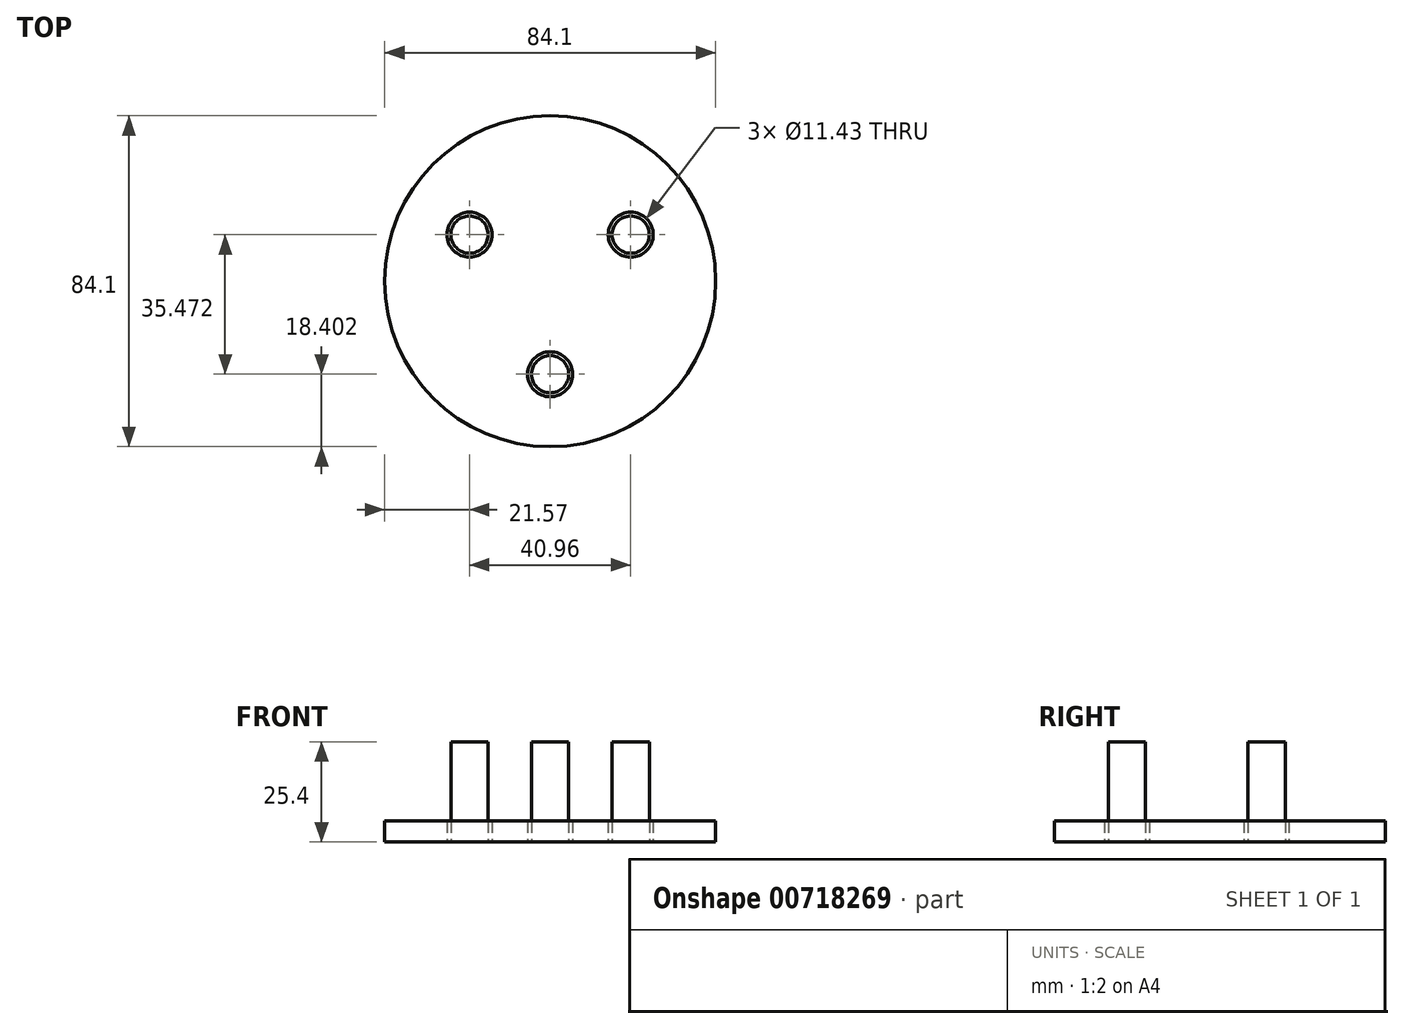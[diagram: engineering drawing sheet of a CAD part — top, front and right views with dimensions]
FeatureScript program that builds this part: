
annotation { "Feature Type Name" : "Feature", "Feature Type Description" : "" }
export const myFeature = defineFeature(function(context is Context, id is Id, definition is map)
    precondition{}
    {
        {
            var Q0;
            Q0=qCreatedBy(makeId("Top.planeOp"),FACE);
            var sketch = newSketch(context, id + "F0", { "sketchPlane" : qUnion([Q0])});
            skCircle(sketch, "E0", {"center": v(0, 0) * mm, "radius": 42.05 * mm});
            skSolve(sketch);
        }
        {
            var Q0;
            Q0=makeQuery(id+"F0.imprint","IMPRINT",FACE,{"disambiguationData":[TD([[makeQuery(id+"F0.imprint","IMPRINT",EDGE,{"derivedFrom":sQuery(id+"F0.wireOp",EDGE,"E0")}),1.0]])]});
            extrude(context, id + "F1", {"entities" : qUnion([Q0]), "depth" : 5.33 * mm, "offsetDistance" : 25.4 * mm});
        }
        {
            var Q0;
            Q0=qCreatedBy(makeId("Top.planeOp"),FACE);
            var sketch = newSketch(context, id + "F2", { "sketchPlane" : qUnion([Q0])});
            skCircle(sketch, "E1", {"center": v(-20.48, 11.82) * mm, "radius": 4.72 * mm});
            skCircle(sketch, "E2.cCircle", {"center": v(0, 0) * mm, "radius": 11.82 * mm, "construction": true});
            skLineSegment(sketch, "E2.0", {"start": v(-20.48, 11.82) * mm, "end": v(20.48, 11.82) * mm, "construction": true});
            skLineSegment(sketch, "E2.1", {"start": v(20.48, 11.82) * mm, "end": v(0, -23.65) * mm, "construction": true});
            skLineSegment(sketch, "E2.2", {"start": v(0, -23.65) * mm, "end": v(-20.48, 11.82) * mm, "construction": true});
            skPoint(sketch, "E2.0.midPoint", {"position": v(0, 11.82) * mm});
            skCircle(sketch, "E3", {"center": v(20.48, 11.82) * mm, "radius": 4.72 * mm});
            skCircle(sketch, "E4", {"center": v(0, -23.65) * mm, "radius": 4.72 * mm});
            skSolve(sketch);
        }
        {
            var Q0;
            Q0=sQuery(id+"F2.wireOp",VERTEX,"E1.center");
            var Q1;
            Q1=sQuery(id+"F2.wireOp",VERTEX,"E2.0.end");
            var Q2;
            Q2=sQuery(id+"F2.wireOp",VERTEX,"E2.2.start");
            var Q3;
            Q3=makeQuery(id+"F1.opExtrude","SWEPT_BODY",BODY,{"disambiguationData":[OSD([sQuery(id+"F0.wireOp",EDGE,"E0")])]});
            hole(context, id + "F3", {"style" : HoleStyle.SIMPLE, "endStyle" : HoleEndStyle.THROUGH, "oppositeDirection" : true, "holeDiameter" : 11.43 * mm, "majorDiameter" : 6.35 * mm, "isTappedThrough" : true, "tappedDepth" : 12.7 * mm, "tapClearance" : 3, "locations" : qUnion([Q0, Q1, Q2]), "scope" : qUnion([Q3])});
        }
        {
            var Q0;
            Q0 = qSketchRegion(id + "F2", true);
            extrude(context, id + "F4", {"entities" : qUnion([Q0]), "depth" : 25.4 * mm, "offsetDistance" : 25.4 * mm});
        }
    });
